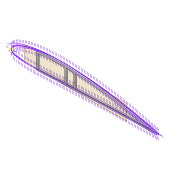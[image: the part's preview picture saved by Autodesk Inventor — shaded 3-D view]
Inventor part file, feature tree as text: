
AUTODESK INVENTOR PART (.ipt)
format: ipt  version: 2022 (Build 260153000, 153)  size: 368,128 bytes
history: native  units: mm
features: extrude x7, sketch x7, projected_geometry x5, shell x1, fillet x1, plane x1
ambient origin geometry x8: Origin, YZ Plane, XZ Plane, XY Plane, X Axis, Y Axis, Z Axis, Center Point
bodies: Solid1 (feature_tree)
feature tree (22):
  extrude  "Extrusion1"  Depth=5.0mm
  shell  "Shell1"  Thickness=2.0mm
  extrude  "Extrusion8"  Depth=5.9mm
  extrude  "Extrusion3"  Depth=10.0mm TaperAngle=0.0deg
  extrude  "Extrusion4"  Depth=2.0mm
  fillet  "Fillet1"  Radius=5.0mm
  extrude  "Extrusion5"  Depth=2.5mm
  plane  "Work Plane2"
  extrude  "Extrusion9"  Depth=1.6mm
  extrude  "Extrusion10"  Depth=0.5mm
  sketch  "Sketch3"  dims[d0=4.0mm d1=0.0mm d2=5.0mm d7=2.0mm]
  sketch  "Sketch8"  dims[d8=2.0mm d9=5.9mm]
  sketch  "Sketch9"  dims[d13=10.0mm d14=0.0mm d16=10.0mm d17=0.0mm]
  sketch  "Sketch10"  dims[d22=4.0mm d23=0.0mm d31=2.0mm d32=5.0mm]
  projected_geometry  "Projected Loop4"
  projected_geometry  "Projected Loop10"
  sketch  "Sketch24"  dims[d34=1.6mm d35=2.5mm]
  projected_geometry  "Projected Loop11"
  projected_geometry  "Projected Loop12"
  sketch  "Sketch26"  dims[d37=5.0mm d38=1.6mm]
  projected_geometry  "Projected Loop13"
  sketch  "Sketch27"  dims[d40=2.5mm d62=72.0mm d63=6.0mm d64=4.0mm d65=0.0mm d66=3.0mm d67=12.0mm d68=75.0mm d69=20.0mm d70=0.5mm d71=10.0mm d72=0.0mm d73=10.0mm d74=0.0mm]
